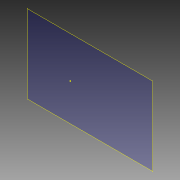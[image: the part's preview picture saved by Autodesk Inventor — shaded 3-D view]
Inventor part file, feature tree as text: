
AUTODESK INVENTOR PART (.ipt)
format: ipt  version: 2014 SP1 (Build 180222100, 222)  size: 56,320 bytes
history: native  units: in
note: dims shown in document units (in); Inventor stores cm internally (conversion verified against a paired STEP export)
features: plane x1, sketch x1
ambient origin geometry x8: Origin, YZ Plane, XZ Plane, XY Plane, X Axis, Y Axis, Z Axis, Center Point
feature tree (2):
  plane  "Work Plane1"
  sketch  "Sketch1"
